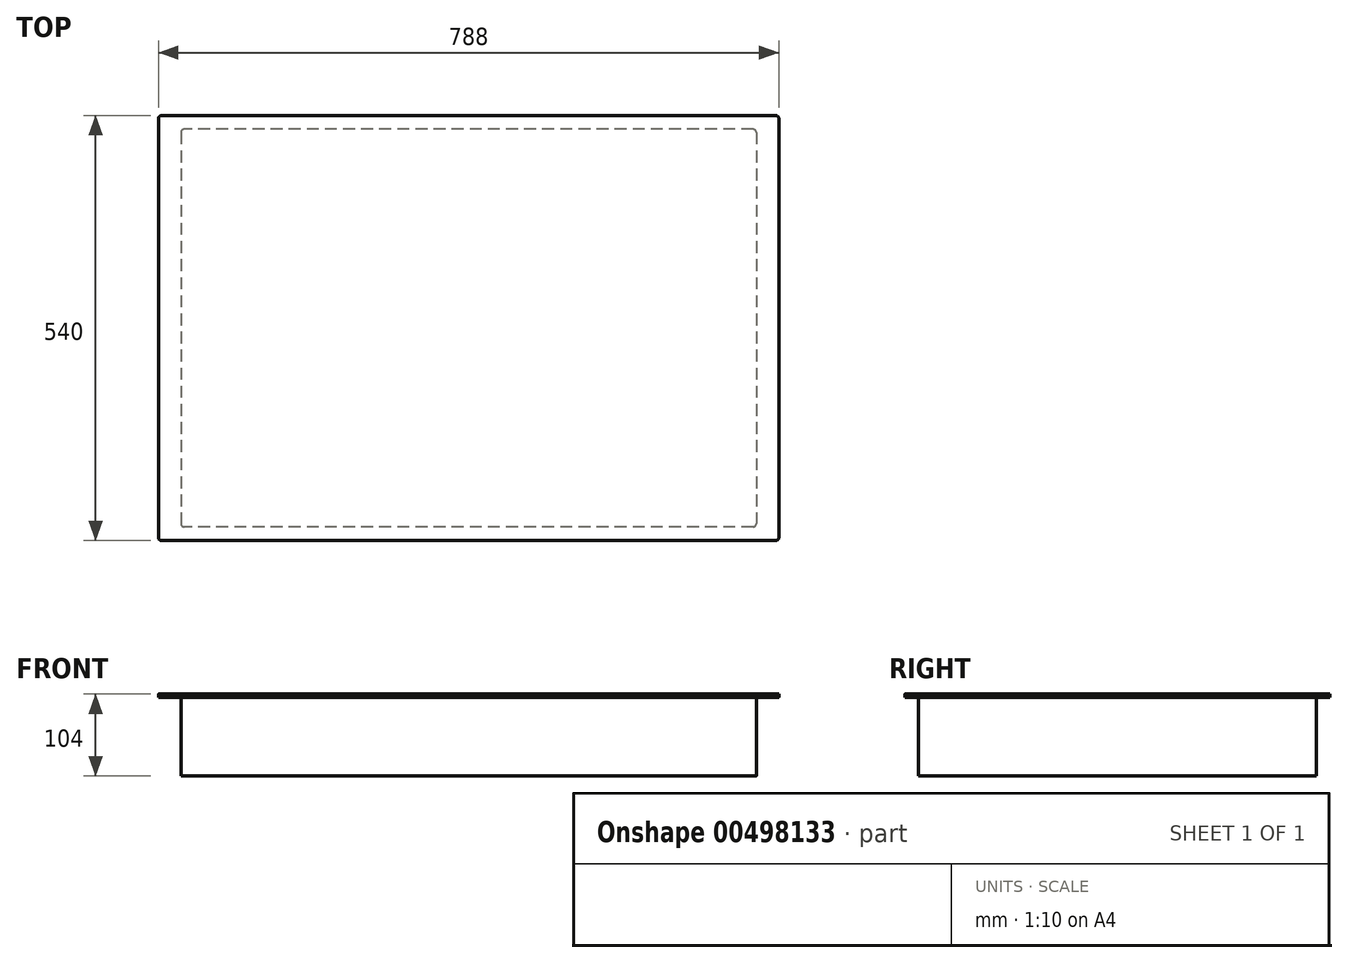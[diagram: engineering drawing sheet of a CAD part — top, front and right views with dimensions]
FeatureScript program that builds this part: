
annotation { "Feature Type Name" : "Feature", "Feature Type Description" : "" }
export const myFeature = defineFeature(function(context is Context, id is Id, definition is map)
    precondition{}
    {
        {
            var Q0;
            Q0=qCreatedBy(makeId("Top.planeOp"),FACE);
            var sketch = newSketch(context, id + "F0", { "sketchPlane" : qUnion([Q0])});
            skLineSegment(sketch, "E0.bottom", {"start": v(365.5, 252.5) * mm, "end": v(-365.5, 252.5) * mm});
            skLineSegment(sketch, "E0.top", {"start": v(365.5, -252.5) * mm, "end": v(-365.5, -252.5) * mm});
            skLineSegment(sketch, "E0.left", {"start": v(365.5, 252.5) * mm, "end": v(365.5, -252.5) * mm});
            skLineSegment(sketch, "E0.right", {"start": v(-365.5, 252.5) * mm, "end": v(-365.5, -252.5) * mm});
            skPoint(sketch, "E0.middle", {"position": v(0, 0) * mm});
            skSolve(sketch);
        }
        {
            var Q0;
            Q0 = qSketchRegion(id + "F0", true);
            extrude(context, id + "F1", {"entities" : qUnion([Q0]), "oppositeDirection" : true, "depth" : 100 * mm});
        }
        {
            var Q0;
            Q0=makeQuery(id+"F1.opExtrude","CAP_FACE",FACE,{"disambiguationData":[OSD([sQuery(id+"F0.wireOp",EDGE,"E0.bottom"),sQuery(id+"F0.wireOp",EDGE,"E0.top"),sQuery(id+"F0.wireOp",EDGE,"E0.left"),sQuery(id+"F0.wireOp",EDGE,"E0.right")])],"isStart":true});
            var sketch = newSketch(context, id + "F2", { "sketchPlane" : qUnion([Q0])});
            skLineSegment(sketch, "E1.bottom", {"start": v(394, 270) * mm, "end": v(-394, 270) * mm});
            skLineSegment(sketch, "E1.top", {"start": v(394, -270) * mm, "end": v(-394, -270) * mm});
            skLineSegment(sketch, "E1.left", {"start": v(394, 270) * mm, "end": v(394, -270) * mm});
            skLineSegment(sketch, "E1.right", {"start": v(-394, 270) * mm, "end": v(-394, -270) * mm});
            skPoint(sketch, "E1.middle", {"position": v(0, 0) * mm});
            skSolve(sketch);
        }
        {
            var Q0;
            Q0 = qSketchRegion(id + "F2", true);
            extrude(context, id + "F3", {"entities" : qUnion([Q0]), "depth" : 4 * mm});
        }
        {
            var Q0;
            Q0=makeQuery(id+"F3.opExtrude","SWEPT_EDGE",EDGE,{"disambiguationData":[OSD([sQuery(id+"F2.wireOp",EDGE,"E1.top"),sQuery(id+"F2.wireOp",EDGE,"E1.right")])]});
            var Q1;
            Q1=makeQuery(id+"F3.opExtrude","SWEPT_EDGE",EDGE,{"disambiguationData":[OSD([sQuery(id+"F2.wireOp",EDGE,"E1.top"),sQuery(id+"F2.wireOp",EDGE,"E1.left")])]});
            var Q2;
            Q2=makeQuery(id+"F3.opExtrude","SWEPT_EDGE",EDGE,{"disambiguationData":[OSD([sQuery(id+"F2.wireOp",EDGE,"E1.bottom"),sQuery(id+"F2.wireOp",EDGE,"E1.left")])]});
            var Q3;
            Q3=makeQuery(id+"F1.opExtrude","SWEPT_EDGE",EDGE,{"disambiguationData":[OSD([sQuery(id+"F0.wireOp",EDGE,"E0.top"),sQuery(id+"F0.wireOp",EDGE,"E0.left")])]});
            var Q4;
            Q4=makeQuery(id+"F1.opExtrude","SWEPT_EDGE",EDGE,{"disambiguationData":[OSD([sQuery(id+"F0.wireOp",EDGE,"E0.bottom"),sQuery(id+"F0.wireOp",EDGE,"E0.left")])]});
            var Q5;
            Q5=makeQuery(id+"F1.opExtrude","SWEPT_EDGE",EDGE,{"disambiguationData":[OSD([sQuery(id+"F0.wireOp",EDGE,"E0.bottom"),sQuery(id+"F0.wireOp",EDGE,"E0.right")])]});
            var Q6;
            Q6=makeQuery(id+"F3.opExtrude","SWEPT_EDGE",EDGE,{"disambiguationData":[OSD([sQuery(id+"F2.wireOp",EDGE,"E1.bottom"),sQuery(id+"F2.wireOp",EDGE,"E1.right")])]});
            var Q7;
            Q7=makeQuery(id+"F1.opExtrude","SWEPT_EDGE",EDGE,{"disambiguationData":[OSD([sQuery(id+"F0.wireOp",EDGE,"E0.top"),sQuery(id+"F0.wireOp",EDGE,"E0.right")])]});
            fillet(context, id + "F4", {"entities" : qUnion([Q0, Q1, Q2, Q3, Q4, Q5, Q6, Q7]), "radius" : 4 * mm, "tangentPropagation" : true, "allowEdgeOverflow" : false});
        }
    });
